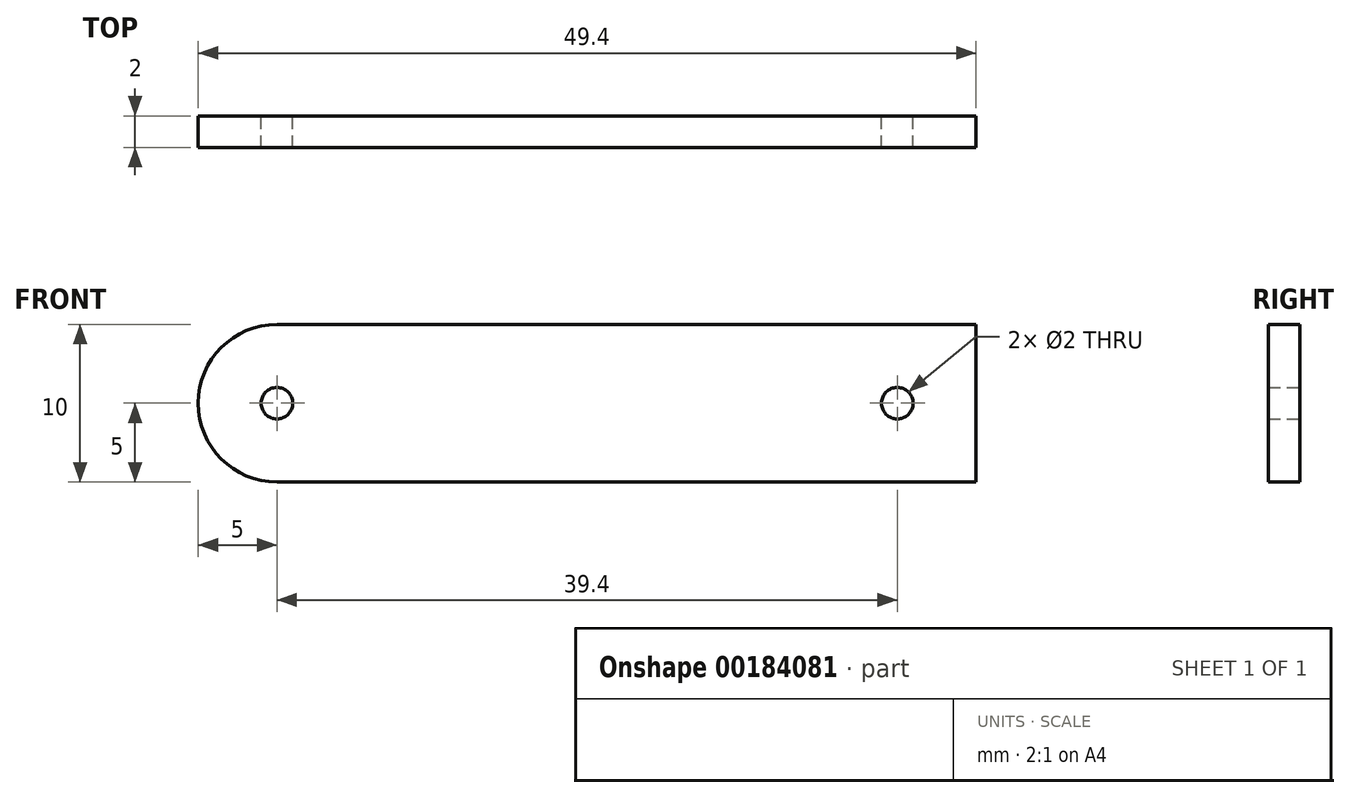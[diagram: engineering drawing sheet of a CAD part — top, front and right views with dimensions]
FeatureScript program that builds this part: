
annotation { "Feature Type Name" : "Feature", "Feature Type Description" : "" }
export const myFeature = defineFeature(function(context is Context, id is Id, definition is map)
    precondition{}
    {
        {
            var Q0;
            Q0=qCreatedBy(makeId("Front.planeOp"),FACE);
            var sketch = newSketch(context, id + "F0", { "sketchPlane" : qUnion([Q0])});
            skLineSegment(sketch, "E0.bottom", {"start": v(0, 0) * mm, "end": v(44.4, 0) * mm});
            skLineSegment(sketch, "E0.top", {"start": v(0, -10) * mm, "end": v(44.4, -10) * mm});
            skLineSegment(sketch, "E0.right", {"start": v(44.4, 0) * mm, "end": v(44.4, -10) * mm});
            skArc(sketch, "E1", {"start": v(0, 0) * mm, "mid": v(-5, -5) * mm, "end": v(0, -10) * mm});
            skCircle(sketch, "E2", {"center": v(0, -5) * mm, "radius": 1 * mm});
            skCircle(sketch, "E3", {"center": v(39.4, -5) * mm, "radius": 1 * mm});
            skSolve(sketch);
        }
        {
            var Q0;
            Q0=makeQuery(id+"F0.imprint","IMPRINT",FACE,{"disambiguationData":[TD([[makeQuery(id+"F0.imprint","IMPRINT",EDGE,{"derivedFrom":sQuery(id+"F0.wireOp",EDGE,"E0.bottom")}),-1.0]])]});
            extrude(context, id + "F1", {"entities" : qUnion([Q0]), "depth" : 2 * mm});
        }
    });
